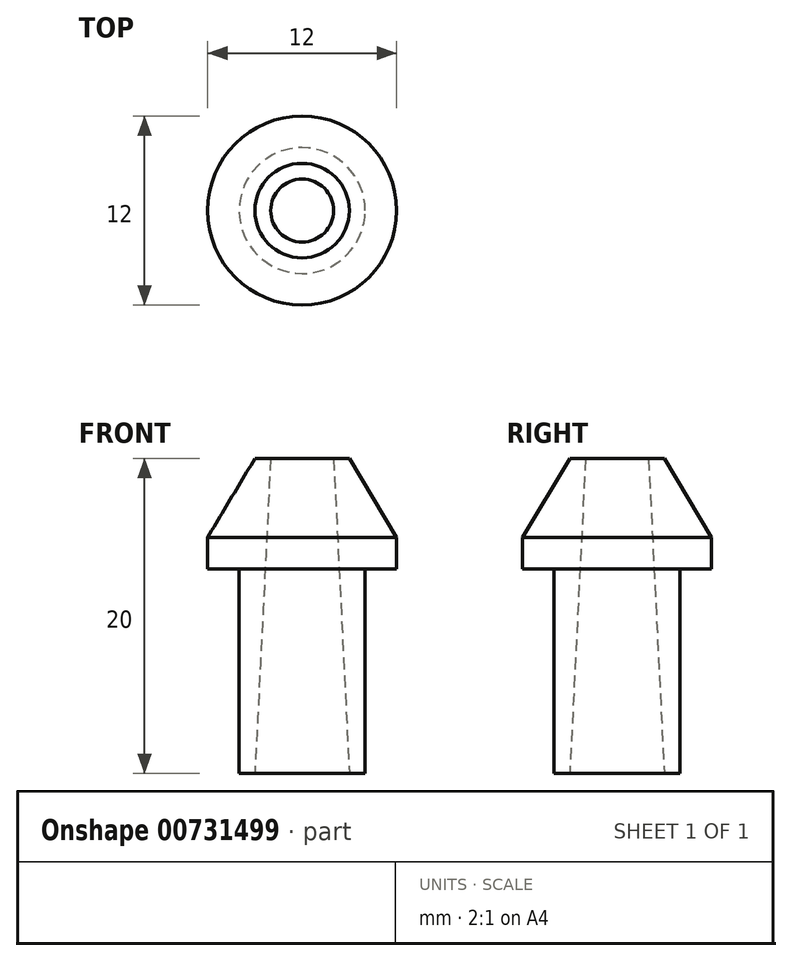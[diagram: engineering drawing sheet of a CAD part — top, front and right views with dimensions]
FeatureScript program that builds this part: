
annotation { "Feature Type Name" : "Feature", "Feature Type Description" : "" }
export const myFeature = defineFeature(function(context is Context, id is Id, definition is map)
    precondition{}
    {
        {
            var Q0;
            Q0=qCreatedBy(makeId("Front.planeOp"),FACE);
            var sketch = newSketch(context, id + "F0", { "sketchPlane" : qUnion([Q0])});
            skLineSegment(sketch, "E0", {"start": v(4, 15) * mm, "end": v(4, 0) * mm});
            skLineSegment(sketch, "E1", {"start": v(2, 20) * mm, "end": v(3, 20) * mm});
            skPoint(sketch, "E1.endSnap0", {"position": v(3, 10) * mm});
            skLineSegment(sketch, "E2", {"start": v(3, 20) * mm, "end": v(4, 15) * mm});
            skLineSegment(sketch, "E3", {"start": v(4, 15) * mm, "end": v(6, 15) * mm});
            skLineSegment(sketch, "E4", {"start": v(6, 15) * mm, "end": v(6, 13) * mm});
            skLineSegment(sketch, "E5", {"start": v(6, 13) * mm, "end": v(4, 13) * mm});
            skLineSegment(sketch, "E6", {"start": v(0, 0) * mm, "end": v(0, 21.16) * mm});
            skLineSegment(sketch, "E7", {"start": v(2, 20) * mm, "end": v(0, 20) * mm});
            skLineSegment(sketch, "E8", {"start": v(4, 0) * mm, "end": v(3, 0) * mm});
            skLineSegment(sketch, "E9", {"start": v(3, 0) * mm, "end": v(2, 20) * mm});
            skLineSegment(sketch, "E10", {"start": v(6, 15) * mm, "end": v(3, 20) * mm});
            skSolve(sketch);
        }
        {
            var Q0;
            Q0=makeQuery(id+"F0.imprint","IMPRINT",FACE,{"disambiguationData":[TD([[makeQuery(id+"F0.imprint","IMPRINT",EDGE,{"derivedFrom":sQuery(id+"F0.wireOp",EDGE,"4Kfo68K4-wx2p-TDYy-YEMi-s4Z4bRHyCwPp")}),1.0]])]});
            var Q1;
            {var subQ0=sQuery(id+"F0.wireOp",EDGE,"E3");Q1=makeQuery(id+"F0.imprint","IMPRINT",FACE,{"disambiguationData":[TD([[makeQuery(id+"F0.imprint","IMPRINT",EDGE,{"derivedFrom":subQ0}),-1.0]])]});}
            var Q2;
            Q2=makeQuery(id+"F0.imprint","IMPRINT",FACE,{"disambiguationData":[TD([[makeQuery(id+"F0.imprint","IMPRINT",EDGE,{"derivedFrom":sQuery(id+"F0.wireOp",EDGE,"E1")}),-1.0]])]});
            var Q3;
            Q3=makeQuery(id+"F0.imprint","IMPRINT",FACE,{"disambiguationData":[TD([[makeQuery(id+"F0.imprint","IMPRINT",EDGE,{"derivedFrom":sQuery(id+"F0.wireOp",EDGE,"E2")}),1.0]])]});
            var Q4;
            Q4=sQuery(id+"F0.wireOp",EDGE,"E6");
            revolve(context, id + "F1", {"surfaceOperationType" : NewSurfaceOperationType.NEW, "entities" : qUnion([Q0, Q1, Q2, Q3]), "axis" : qUnion([Q4]), "revolveType" : RevolveType.FULL});
        }
    });
